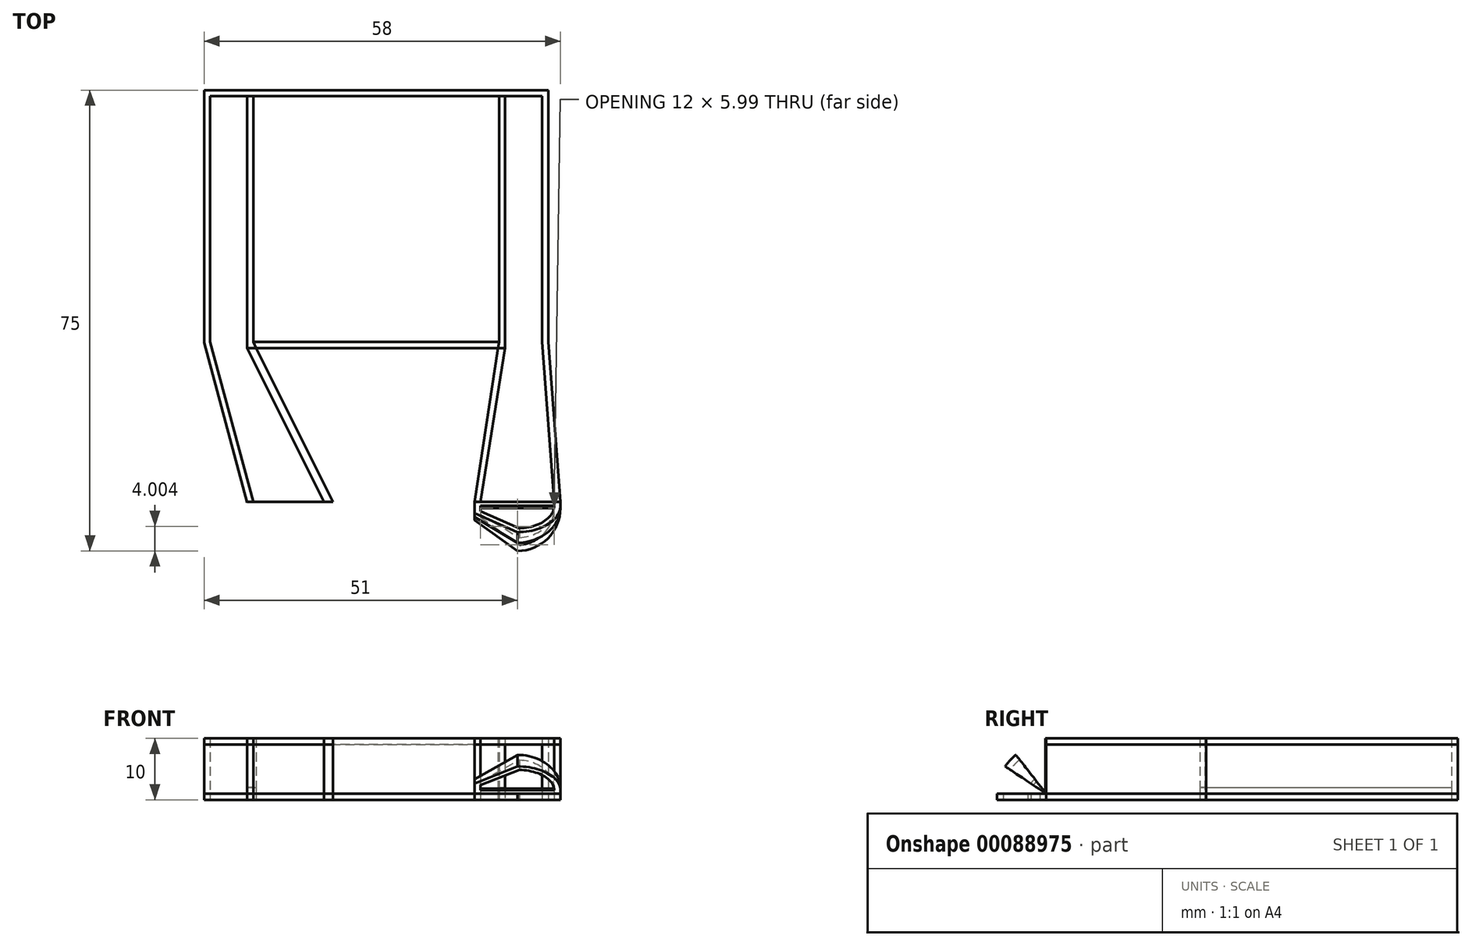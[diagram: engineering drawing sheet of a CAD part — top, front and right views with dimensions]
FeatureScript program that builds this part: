
annotation { "Feature Type Name" : "Feature", "Feature Type Description" : "" }
export const myFeature = defineFeature(function(context is Context, id is Id, definition is map)
    precondition{}
    {
        {
            var Q0;
            Q0=qCreatedBy(makeId("Top.planeOp"),FACE);
            var sketch = newSketch(context, id + "F0", { "sketchPlane" : qUnion([Q0])});
            skLineSegment(sketch, "E0.bottom", {"start": v(0, 0) * mm, "end": v(40, 0) * mm});
            skLineSegment(sketch, "E0.top", {"start": v(0, 40) * mm, "end": v(40, 40) * mm});
            skLineSegment(sketch, "E0.left", {"start": v(0, 0) * mm, "end": v(0, 40) * mm});
            skLineSegment(sketch, "E0.right", {"start": v(40, 0) * mm, "end": v(40, 40) * mm});
            skLineSegment(sketch, "E1.top", {"start": v(-1, -11) * mm, "end": v(49, -11) * mm, "construction": true});
            skLineSegment(sketch, "E2.bottom", {"start": v(-1, -11) * mm, "end": v(0, -11) * mm});
            skLineSegment(sketch, "E2.top", {"start": v(-1, -26) * mm, "end": v(13, -26) * mm});
            skLineSegment(sketch, "E2.left", {"start": v(-1, -11) * mm, "end": v(-1, -26) * mm, "construction": true});
            skLineSegment(sketch, "E2.right", {"start": v(13, -11) * mm, "end": v(13, -26) * mm, "construction": true});
            skLineSegment(sketch, "E3.bottom", {"start": v(50, -11) * mm, "end": v(49, -11) * mm, "construction": true});
            skLineSegment(sketch, "E3.top", {"start": v(50, -26) * mm, "end": v(36, -26) * mm});
            skLineSegment(sketch, "E3.left", {"start": v(50, -11) * mm, "end": v(50, -26) * mm, "construction": true});
            skLineSegment(sketch, "E3.right", {"start": v(36, -11) * mm, "end": v(36, -26) * mm, "construction": true});
            skLineSegment(sketch, "E4", {"start": v(13, -26) * mm, "end": v(13, -29) * mm});
            skLineSegment(sketch, "E5", {"start": v(36, -26) * mm, "end": v(36, -29) * mm});
            skLineSegment(sketch, "E6.0", {"start": v(-1, -27) * mm, "end": v(13, -27) * mm});
            skLineSegment(sketch, "E7.0", {"start": v(50, -27) * mm, "end": v(36, -27) * mm});
            skPoint(sketch, "E8", {"position": v(6, -27) * mm});
            skArc(sketch, "E9", {"start": v(-1, -27) * mm, "mid": v(1.05, -31.95) * mm, "end": v(6, -34) * mm});
            skLineSegment(sketch, "E10", {"start": v(13, -29) * mm, "end": v(6, -34) * mm});
            skLineSegment(sketch, "E11", {"start": v(-1, -26) * mm, "end": v(-1, -27) * mm});
            skPoint(sketch, "E12", {"position": v(43, -27) * mm});
            skArc(sketch, "E13", {"start": v(50, -27) * mm, "mid": v(47.95, -31.95) * mm, "end": v(43, -34) * mm});
            skLineSegment(sketch, "E14", {"start": v(36, -29) * mm, "end": v(43, -34) * mm});
            skLineSegment(sketch, "E15", {"start": v(50, -26) * mm, "end": v(50, -27) * mm});
            skLineSegment(sketch, "E16", {"start": v(0, -11) * mm, "end": v(0, -26) * mm, "construction": true});
            skLineSegment(sketch, "E17", {"start": v(0, -26) * mm, "end": v(0, -27) * mm});
            skLineSegment(sketch, "E18.1", {"start": v(12, -28.49) * mm, "end": v(5.7, -33) * mm});
            skArc(sketch, "E18.2", {"start": v(0, -27) * mm, "mid": v(1.65, -31.13) * mm, "end": v(5.7, -33) * mm});
            skArc(sketch, "E19.0", {"start": v(49, -27) * mm, "mid": v(47.35, -31.13) * mm, "end": v(43.3, -33) * mm});
            skLineSegment(sketch, "E19.1", {"start": v(37, -28.49) * mm, "end": v(43.3, -33) * mm});
            skLineSegment(sketch, "E20", {"start": v(49, -27) * mm, "end": v(49, -26) * mm});
            skLineSegment(sketch, "E21", {"start": v(49, -26) * mm, "end": v(49, -11) * mm, "construction": true});
            skLineSegment(sketch, "E22", {"start": v(12, -26) * mm, "end": v(12, -27) * mm});
            skLineSegment(sketch, "E23", {"start": v(37, -27) * mm, "end": v(37, -28.49) * mm});
            skLineSegment(sketch, "E24", {"start": v(37, -26) * mm, "end": v(37, -27) * mm});
            skLineSegment(sketch, "E25", {"start": v(12, -26) * mm, "end": v(12, -11) * mm, "construction": true});
            skLineSegment(sketch, "E26", {"start": v(37, -26) * mm, "end": v(37, -11) * mm, "construction": true});
            skLineSegment(sketch, "E27", {"start": v(0, -11) * mm, "end": v(0, -11) * mm});
            skLineSegment(sketch, "E28", {"start": v(49, -11) * mm, "end": v(36, -11) * mm, "construction": true});
            skLineSegment(sketch, "E29", {"start": v(49, -11) * mm, "end": v(50, -11) * mm, "construction": true});
            skLineSegment(sketch, "E30", {"start": v(0, -11) * mm, "end": v(13, -11) * mm});
            skLineSegment(sketch, "E31", {"start": v(0, -10) * mm, "end": v(49, -10) * mm, "construction": true});
            skLineSegment(sketch, "E32.0", {"start": v(-1, 41) * mm, "end": v(41, 41) * mm});
            skLineSegment(sketch, "E32.1", {"start": v(-1, -1) * mm, "end": v(-1, 41) * mm});
            skLineSegment(sketch, "E32.2", {"start": v(-1, -1) * mm, "end": v(41, -1) * mm});
            skLineSegment(sketch, "E32.3", {"start": v(41, -1) * mm, "end": v(41, 41) * mm});
            skLineSegment(sketch, "E33", {"start": v(0, 40) * mm, "end": v(-7, 40) * mm});
            skLineSegment(sketch, "E34", {"start": v(-7, 40) * mm, "end": v(-7, 0) * mm});
            skLineSegment(sketch, "E35", {"start": v(-7, 0) * mm, "end": v(0, -26) * mm});
            skLineSegment(sketch, "E36", {"start": v(0, 0) * mm, "end": v(13, -26) * mm});
            skLineSegment(sketch, "E37", {"start": v(-1, -1) * mm, "end": v(12, -27) * mm});
            skLineSegment(sketch, "E38", {"start": v(12, -28.49) * mm, "end": v(12, -27) * mm});
            skLineSegment(sketch, "E39.0", {"start": v(-8, -0.13) * mm, "end": v(-0.97, -26.26) * mm});
            skLineSegment(sketch, "E39.1", {"start": v(-8, 41) * mm, "end": v(-8, -0.13) * mm});
            skLineSegment(sketch, "E39.2", {"start": v(0, 41) * mm, "end": v(-8, 41) * mm});
            skLineSegment(sketch, "E40", {"start": v(40, 40) * mm, "end": v(47, 40) * mm});
            skLineSegment(sketch, "E41", {"start": v(47, 40) * mm, "end": v(47, 0) * mm});
            skLineSegment(sketch, "E42", {"start": v(47, 0) * mm, "end": v(49, -26) * mm});
            skLineSegment(sketch, "E43", {"start": v(40, 0) * mm, "end": v(36, -26) * mm});
            skLineSegment(sketch, "E44", {"start": v(41, -1) * mm, "end": v(37, -26) * mm});
            skLineSegment(sketch, "E45.0", {"start": v(48, 0.04) * mm, "end": v(50, -25.92) * mm});
            skLineSegment(sketch, "E45.1", {"start": v(48, 41) * mm, "end": v(48, 0.04) * mm});
            skLineSegment(sketch, "E45.2", {"start": v(40, 41) * mm, "end": v(48, 41) * mm});
            skLineSegment(sketch, "E46", {"start": v(48, 0.04) * mm, "end": v(50, -26) * mm});
            skLineSegment(sketch, "E47", {"start": v(12, -28.49) * mm, "end": v(13, -29) * mm});
            skLineSegment(sketch, "E48", {"start": v(5.7, -33) * mm, "end": v(6, -34) * mm});
            skLineSegment(sketch, "E49", {"start": v(37, -28.49) * mm, "end": v(36, -29) * mm});
            skLineSegment(sketch, "E50", {"start": v(43.3, -33) * mm, "end": v(43, -34) * mm});
            skSolve(sketch);
        }
        {
            var Q0;
            {var subQ11=sQuery(id+"F0.wireOp",EDGE,"E0.top");Q0=makeQuery(id+"F0.imprint","IMPRINT",FACE,{"disambiguationData":[TD([[makeQuery(id+"F0.imprint","IMPRINT",EDGE,{"derivedFrom":subQ11}),1.0]])]});}
            var Q1;
            {var subQ1=sQuery(id+"F0.wireOp",EDGE,"E0.left");Q1=makeQuery(id+"F0.imprint","IMPRINT",FACE,{"disambiguationData":[TD([[makeQuery(id+"F0.imprint","IMPRINT",EDGE,{"derivedFrom":subQ1}),1.0]])]});}
            var Q2;
            {var subQ0=sQuery(id+"F0.wireOp",EDGE,"E34");Q2=makeQuery(id+"F0.imprint","IMPRINT",FACE,{"disambiguationData":[TD([[makeQuery(id+"F0.imprint","IMPRINT",EDGE,{"derivedFrom":subQ0}),-1.0]])]});}
            var Q3;
            {var subQ0=sQuery(id+"F0.wireOp",EDGE,"E34");Q3=makeQuery(id+"F0.imprint","IMPRINT",FACE,{"disambiguationData":[TD([[makeQuery(id+"F0.imprint","IMPRINT",EDGE,{"derivedFrom":subQ0}),1.0]])]});}
            var Q4;
            {var subQ0=sQuery(id+"F0.wireOp",EDGE,"E41");Q4=makeQuery(id+"F0.imprint","IMPRINT",FACE,{"disambiguationData":[TD([[makeQuery(id+"F0.imprint","IMPRINT",EDGE,{"derivedFrom":subQ0}),-1.0]])]});}
            var Q5;
            {var subQ1=sQuery(id+"F0.wireOp",EDGE,"E0.right");Q5=makeQuery(id+"F0.imprint","IMPRINT",FACE,{"disambiguationData":[TD([[makeQuery(id+"F0.imprint","IMPRINT",EDGE,{"derivedFrom":subQ1}),-1.0]])]});}
            var Q6;
            {var subQ0=sQuery(id+"F0.wireOp",EDGE,"E41");Q6=makeQuery(id+"F0.imprint","IMPRINT",FACE,{"disambiguationData":[TD([[makeQuery(id+"F0.imprint","IMPRINT",EDGE,{"derivedFrom":subQ0}),1.0]])]});}
            var Q7;
            {var subQ0=sQuery(id+"F0.wireOp",EDGE,"E0.bottom");Q7=makeQuery(id+"F0.imprint","IMPRINT",FACE,{"disambiguationData":[TD([[makeQuery(id+"F0.imprint","IMPRINT",EDGE,{"derivedFrom":subQ0}),-1.0]])]});}
            var Q8;
            {var subQ3=sQuery(id+"F0.wireOp",EDGE,"E44");Q8=makeQuery(id+"F0.imprint","IMPRINT",FACE,{"disambiguationData":[TD([[makeQuery(id+"F0.imprint","IMPRINT",EDGE,{"derivedFrom":subQ3}),-1.0]])]});}
            var Q9;
            {var subQ0=sQuery(id+"F0.wireOp",EDGE,"E36");var subQ1=sQuery(id+"F0.wireOp",EDGE,"E30");var subQ2=makeQuery(id+"F0.imprint","INTERSECT",VERTEX,{"derivedFrom":[subQ1,subQ0]});Q9=makeQuery(id+"F0.imprint","IMPRINT",FACE,{"disambiguationData":[TD([[makeQuery(id+"F0.imprint","IMPRINT",EDGE,{"disambiguationData":[TD([[subQ2,1.0]])],"derivedFrom":subQ1}),1.0]])]});}
            var Q10;
            {var subQ1=sQuery(id+"F0.wireOp",EDGE,"E2.top");var subQ7=makeQuery(id+"F0.imprint","INTERSECT",VERTEX,{"derivedFrom":[subQ1,sQuery(id+"F0.wireOp",EDGE,"E22")]});Q10=makeQuery(id+"F0.imprint","IMPRINT",FACE,{"disambiguationData":[TD([[makeQuery(id+"F0.imprint","IMPRINT",EDGE,{"disambiguationData":[TD([[subQ7,1.0]])],"derivedFrom":subQ1}),1.0]])]});}
            extrude(context, id + "F1", {"entities" : qUnion([Q0, Q1, Q2, Q3, Q4, Q5, Q6, Q7, Q8, Q9, Q10]), "depth" : 1 * mm});
        }
        {
            var Q0;
            {var subQ1=sQuery(id+"F0.wireOp",EDGE,"E0.left");Q0=makeQuery(id+"F0.imprint","IMPRINT",FACE,{"disambiguationData":[TD([[makeQuery(id+"F0.imprint","IMPRINT",EDGE,{"derivedFrom":subQ1}),1.0]])]});}
            var Q1;
            {var subQ1=sQuery(id+"F0.wireOp",EDGE,"E0.right");Q1=makeQuery(id+"F0.imprint","IMPRINT",FACE,{"disambiguationData":[TD([[makeQuery(id+"F0.imprint","IMPRINT",EDGE,{"derivedFrom":subQ1}),-1.0]])]});}
            extrude(context, id + "F2", {"entities" : qUnion([Q0, Q1]), "operationType" : NewBodyOperationType.ADD, "depth" : 2 * mm});
        }
        {
            var Q0;
            {var subQ0=sQuery(id+"F0.wireOp",EDGE,"E34");Q0=makeQuery(id+"F0.imprint","IMPRINT",FACE,{"disambiguationData":[TD([[makeQuery(id+"F0.imprint","IMPRINT",EDGE,{"derivedFrom":subQ0}),-1.0]])]});}
            var Q1;
            {var subQ11=sQuery(id+"F0.wireOp",EDGE,"E0.top");Q1=makeQuery(id+"F0.imprint","IMPRINT",FACE,{"disambiguationData":[TD([[makeQuery(id+"F0.imprint","IMPRINT",EDGE,{"derivedFrom":subQ11}),1.0]])]});}
            var Q2;
            {var subQ0=sQuery(id+"F0.wireOp",EDGE,"E41");Q2=makeQuery(id+"F0.imprint","IMPRINT",FACE,{"disambiguationData":[TD([[makeQuery(id+"F0.imprint","IMPRINT",EDGE,{"derivedFrom":subQ0}),1.0]])]});}
            var Q3;
            {var subQ0=sQuery(id+"F0.wireOp",EDGE,"E0.bottom");Q3=makeQuery(id+"F0.imprint","IMPRINT",FACE,{"disambiguationData":[TD([[makeQuery(id+"F0.imprint","IMPRINT",EDGE,{"derivedFrom":subQ0}),-1.0]])]});}
            var Q4;
            {var subQ0=sQuery(id+"F0.wireOp",EDGE,"E36");var subQ1=sQuery(id+"F0.wireOp",EDGE,"E30");var subQ2=makeQuery(id+"F0.imprint","INTERSECT",VERTEX,{"derivedFrom":[subQ1,subQ0]});Q4=makeQuery(id+"F0.imprint","IMPRINT",FACE,{"disambiguationData":[TD([[makeQuery(id+"F0.imprint","IMPRINT",EDGE,{"disambiguationData":[TD([[subQ2,1.0]])],"derivedFrom":subQ1}),1.0]])]});}
            var Q5;
            {var subQ3=sQuery(id+"F0.wireOp",EDGE,"E44");Q5=makeQuery(id+"F0.imprint","IMPRINT",FACE,{"disambiguationData":[TD([[makeQuery(id+"F0.imprint","IMPRINT",EDGE,{"derivedFrom":subQ3}),-1.0]])]});}
            var Q6;
            {var subQ1=sQuery(id+"F0.wireOp",EDGE,"E2.top");var subQ7=makeQuery(id+"F0.imprint","INTERSECT",VERTEX,{"derivedFrom":[subQ1,sQuery(id+"F0.wireOp",EDGE,"E22")]});Q6=makeQuery(id+"F0.imprint","IMPRINT",FACE,{"disambiguationData":[TD([[makeQuery(id+"F0.imprint","IMPRINT",EDGE,{"disambiguationData":[TD([[subQ7,1.0]])],"derivedFrom":subQ1}),1.0]])]});}
            extrude(context, id + "F3", {"entities" : qUnion([Q0, Q1, Q2, Q3, Q4, Q5, Q6]), "depth" : 10 * mm});
        }
        {
            var Q0;
            Q0=makeQuery(id+"F2.opExtrude","CAP_FACE",FACE,{"disambiguationData":[OSD([sQuery(id+"F0.wireOp",EDGE,"E0.left"),sQuery(id+"F0.wireOp",EDGE,"E32.1"),sQuery(id+"F0.wireOp",EDGE,"E32.2"),sQuery(id+"F0.wireOp",EDGE,"E33"),sQuery(id+"F0.wireOp",EDGE,"E36")])],"isStart":false});
            var Q1;
            Q1=makeQuery(id+"F2.opExtrude","CAP_FACE",FACE,{"disambiguationData":[OSD([sQuery(id+"F0.wireOp",EDGE,"E0.right"),sQuery(id+"F0.wireOp",EDGE,"E32.2"),sQuery(id+"F0.wireOp",EDGE,"E32.3"),sQuery(id+"F0.wireOp",EDGE,"E40"),sQuery(id+"F0.wireOp",EDGE,"E43")])],"isStart":false});
            var Q2;
            Q2=makeQuery(id+"F3.opExtrude","CAP_FACE",FACE,{"disambiguationData":[OSD([sQuery(id+"F0.wireOp",EDGE,"E0.top"),sQuery(id+"F0.wireOp",EDGE,"E2.top"),sQuery(id+"F0.wireOp",EDGE,"E3.top"),sQuery(id+"F0.wireOp",EDGE,"E11"),sQuery(id+"F0.wireOp",EDGE,"E32.0"),sQuery(id+"F0.wireOp",EDGE,"E33"),sQuery(id+"F0.wireOp",EDGE,"E34"),sQuery(id+"F0.wireOp",EDGE,"E35"),sQuery(id+"F0.wireOp",EDGE,"E39.0"),sQuery(id+"F0.wireOp",EDGE,"E39.1"),sQuery(id+"F0.wireOp",EDGE,"E39.2"),sQuery(id+"F0.wireOp",EDGE,"E40"),sQuery(id+"F0.wireOp",EDGE,"E41"),sQuery(id+"F0.wireOp",EDGE,"E42"),sQuery(id+"F0.wireOp",EDGE,"E45.2"),sQuery(id+"F0.wireOp",EDGE,"E45.1"),sQuery(id+"F0.wireOp",EDGE,"E46")])],"isStart":false});
            extrude(context, id + "F4", {"entities" : qUnion([Q0, Q1]), "endBound" : BoundingType.UP_TO_SURFACE, "endBoundEntityFace" : qUnion([Q2]), "depth" : 25 * mm, "hasSecondDirection" : true, "secondDirectionOppositeDirection" : false, "secondDirectionDepth" : 7 * mm});
        }
        {
            var Q0;
            {var subQ0=sQuery(id+"F0.wireOp",EDGE,"E0.top");var subQ2=sQuery(id+"F0.wireOp",EDGE,"E32.2");var subQ4=sQuery(id+"F0.wireOp",EDGE,"E36");var subQ5=sQuery(id+"F0.wireOp",EDGE,"E2.top");var subQ6=sQuery(id+"F0.wireOp",EDGE,"E0.right");var subQ7=sQuery(id+"F0.wireOp",EDGE,"E45.1");var subQ8=sQuery(id+"F0.wireOp",EDGE,"E0.left");var subQ9=sQuery(id+"F0.wireOp",EDGE,"E45.2");var subQ10=sQuery(id+"F0.wireOp",EDGE,"E39.2");var subQ11=sQuery(id+"F0.wireOp",EDGE,"E32.0");var subQ12=sQuery(id+"F0.wireOp",EDGE,"E43");var subQ13=sQuery(id+"F0.wireOp",EDGE,"E39.0");var subQ14=sQuery(id+"F0.wireOp",EDGE,"E3.top");var subQ15=sQuery(id+"F0.wireOp",EDGE,"E39.1");var subQ16=sQuery(id+"F0.wireOp",EDGE,"E46");var subQ17=sQuery(id+"F0.wireOp",EDGE,"E11");var subQ18=makeQuery(id+"F1.opExtrude","CAP_FACE",FACE,{"disambiguationData":[OSD([sQuery(id+"F0.wireOp",EDGE,"E0.bottom"),subQ0,subQ8,subQ6,subQ5,subQ14,subQ17,subQ11,subQ2,subQ4,subQ13,subQ15,subQ10,subQ12,subQ9,subQ7,subQ16])],"isStart":false});Q0=makeQuery(id+"F2.boolean.opBoolean","SPLIT",FACE,{"disambiguationData":[TD([makeQuery(id+"F1.opExtrude","SWEPT_FACE",FACE,{"disambiguationData":[OSD([subQ0])]})])],"derivedFrom":subQ18});}
            var Q1;
            Q1=makeQuery(id+"F3.opExtrude","CAP_FACE",FACE,{"disambiguationData":[OSD([sQuery(id+"F0.wireOp",EDGE,"E0.top"),sQuery(id+"F0.wireOp",EDGE,"E2.top"),sQuery(id+"F0.wireOp",EDGE,"E3.top"),sQuery(id+"F0.wireOp",EDGE,"E11"),sQuery(id+"F0.wireOp",EDGE,"E32.0"),sQuery(id+"F0.wireOp",EDGE,"E33"),sQuery(id+"F0.wireOp",EDGE,"E34"),sQuery(id+"F0.wireOp",EDGE,"E35"),sQuery(id+"F0.wireOp",EDGE,"E39.0"),sQuery(id+"F0.wireOp",EDGE,"E39.1"),sQuery(id+"F0.wireOp",EDGE,"E39.2"),sQuery(id+"F0.wireOp",EDGE,"E40"),sQuery(id+"F0.wireOp",EDGE,"E41"),sQuery(id+"F0.wireOp",EDGE,"E42"),sQuery(id+"F0.wireOp",EDGE,"E45.2"),sQuery(id+"F0.wireOp",EDGE,"E45.1"),sQuery(id+"F0.wireOp",EDGE,"E46")])],"isStart":false});
            var Q2;
            Q2=makeQuery(id+"F3.opExtrude","SWEPT_BODY",BODY,{"disambiguationData":[OSD([sQuery(id+"F0.wireOp",EDGE,"E0.top"),sQuery(id+"F0.wireOp",EDGE,"E2.top"),sQuery(id+"F0.wireOp",EDGE,"E3.top"),sQuery(id+"F0.wireOp",EDGE,"E11"),sQuery(id+"F0.wireOp",EDGE,"E32.0"),sQuery(id+"F0.wireOp",EDGE,"E33"),sQuery(id+"F0.wireOp",EDGE,"E34"),sQuery(id+"F0.wireOp",EDGE,"E35"),sQuery(id+"F0.wireOp",EDGE,"E39.0"),sQuery(id+"F0.wireOp",EDGE,"E39.1"),sQuery(id+"F0.wireOp",EDGE,"E39.2"),sQuery(id+"F0.wireOp",EDGE,"E40"),sQuery(id+"F0.wireOp",EDGE,"E41"),sQuery(id+"F0.wireOp",EDGE,"E42"),sQuery(id+"F0.wireOp",EDGE,"E45.2"),sQuery(id+"F0.wireOp",EDGE,"E45.1"),sQuery(id+"F0.wireOp",EDGE,"E46")])]});
            extrude(context, id + "F5", {"entities" : qUnion([Q0]), "endBound" : BoundingType.UP_TO_SURFACE, "endBoundEntityFace" : qUnion([Q1]), "endBoundEntityBody" : qUnion([Q2]), "depth" : 25 * mm, "hasSecondDirection" : true, "secondDirectionOppositeDirection" : false, "secondDirectionDepth" : 8 * mm});
        }
        {
            var Q0;
            {var subQ0=sQuery(id+"F0.wireOp",EDGE,"E20");Q0=makeQuery(id+"F0.imprint","IMPRINT",FACE,{"disambiguationData":[TD([[makeQuery(id+"F0.imprint","IMPRINT",EDGE,{"derivedFrom":subQ0}),1.0]])]});}
            var Q1;
            {var subQ3=sQuery(id+"F0.wireOp",EDGE,"E24");Q1=makeQuery(id+"F0.imprint","IMPRINT",FACE,{"disambiguationData":[TD([[makeQuery(id+"F0.imprint","IMPRINT",EDGE,{"derivedFrom":subQ3}),-1.0]])]});}
            var Q2;
            {var subQ4=sQuery(id+"F0.wireOp",EDGE,"E23");Q2=makeQuery(id+"F0.imprint","IMPRINT",FACE,{"disambiguationData":[TD([[makeQuery(id+"F0.imprint","IMPRINT",EDGE,{"derivedFrom":subQ4}),-1.0]])]});}
            var Q3;
            {var subQ0=sQuery(id+"F0.wireOp",EDGE,"E15");Q3=makeQuery(id+"F0.imprint","IMPRINT",FACE,{"disambiguationData":[TD([[makeQuery(id+"F0.imprint","IMPRINT",EDGE,{"derivedFrom":subQ0}),-1.0]])]});}
            var Q4;
            {var subQ0=sQuery(id+"F0.wireOp",EDGE,"E19.0");Q4=makeQuery(id+"F0.imprint","IMPRINT",FACE,{"disambiguationData":[TD([[makeQuery(id+"F0.imprint","IMPRINT",EDGE,{"derivedFrom":subQ0}),-1.0]])]});}
            var Q5;
            {var subQ0=sQuery(id+"F0.wireOp",EDGE,"E13");Q5=makeQuery(id+"F0.imprint","IMPRINT",FACE,{"disambiguationData":[TD([[makeQuery(id+"F0.imprint","IMPRINT",EDGE,{"derivedFrom":subQ0}),-1.0]])]});}
            var Q6;
            Q6=makeQuery(id+"F0.imprint","IMPRINT",FACE,{"disambiguationData":[TD([[makeQuery(id+"F0.imprint","IMPRINT",EDGE,{"derivedFrom":sQuery(id+"F0.wireOp",EDGE,"E14")}),1.0]])]});
            extrude(context, id + "F6", {"entities" : qUnion([Q0, Q1, Q2, Q3, Q4, Q5, Q6]), "depth" : 1 * mm});
        }
        {
            var Q0;
            Q0=makeQuery(id+"F6.opExtrude","CAP_FACE",FACE,{"disambiguationData":[OSD([sQuery(id+"F0.wireOp",EDGE,"E3.top"),sQuery(id+"F0.wireOp",EDGE,"E5"),sQuery(id+"F0.wireOp",EDGE,"E13"),sQuery(id+"F0.wireOp",EDGE,"E14"),sQuery(id+"F0.wireOp",EDGE,"E15")])],"isStart":false});
            var Q1;
            Q1=makeQuery(id+"F6.opExtrude","CAP_EDGE",EDGE,{"disambiguationData":[OSD([sQuery(id+"F0.wireOp",EDGE,"E3.top")])],"isStart":false});
            revolve(context, id + "F7", {"entities" : qUnion([Q0]), "axis" : qUnion([Q1]), "revolveType" : RevolveType.TWO_DIRECTIONS, "angle" : 51.94 * degree, "angleBack" : 33.6 * degree});
        }
    });
